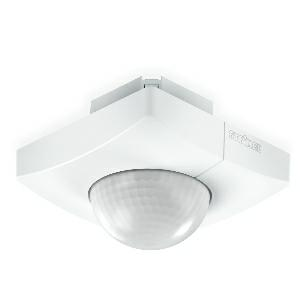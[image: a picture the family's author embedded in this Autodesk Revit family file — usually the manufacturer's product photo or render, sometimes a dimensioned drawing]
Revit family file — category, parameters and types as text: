
# Revit family: is_3360_057244
name_source: partatom
category: Elektroinstallationen
revit_build: Autodesk Revit 2016 (Build: 20190508_0715(x64)
units: mm (PartAtom-declared; Revit-internal decimal feet)

## family parameters
Basisbauteil = Fläche
Beim Laden mit Abzugskörper schneiden = Nein
Bemaßung runder Anschluss = Durchmesser verwenden
Beschriftungsausrichtung beibehalten = Nein
Gemeinsam genutzt = Nein
Raumberechnungspunkt = Nein
Teiletyp = Normal

## types (1)
- IS 3360
    Apparent Load = 0 VA
    Beschreibung = Type: Motion detectors; Dimensions (L x W x H): 78 x 94 x 94 mm; Mains power supply: 12 – 22,5 V / 50 – 60 Hz; Sensor Technology: passive infrared; Application, place: Indoors; Application, room: production facilities, recreation room, changing room, function room / ancillary room, sports hall, reception / lobby, stairwell, WC / washroom, multi-storey / underground car park, warehouse, Indoors; Installation site: ceiling; Installation: Concealed wiring; Switching zones: 448 switching zones; Electronic scalability: No; Mechanical scalability: No; Mounting height: 2,5 – 4,00 m; Optimum mounting height: 2,8 m; Detection angle: 360 °; Angle of aperture: 45 °; Sneak-by guard: Yes; Capability of masking out individual segments: Yes; Reach, radial: Ø 8 m (50 m²); Reach, tangential: Ø 40 m (1257 m²); Reach, presence: Ø 3 m (7 m²); Twilight setting TEACH: Yes; Twilight setting: 2 – 1000 lx; Switching output 1, floating: No; Control output, Dali: Addressable/slave; Basic light level function: No; With bus coupling: Yes; Settings via: Bus; With remote control: No; Interconnection: Yes; IP-rating: IP20; Material: Plastic; Ambient temperature: -20 – 50 °C; Colour: white; Colour, RAL: 9003; Manufacturer's Warranty: 5 years; Version: DALI-2 IPD - concealed, sq.; PU1, EAN: 4007841057244
    Height = 0 mm  [stored 0 ft]
    Hersteller = Steinel
    Length = 78 mm  [stored 0.255906 ft]
    Maximum range = 20.158 m
    ModVariant = Nein
    Modell = 057244
    Mounting Place = Ceiling
    Mounting Type = Recessed
    Number of Poles = 1
    OnlyDefault = Ja
    Power Factor = 1
    Product Name = IS 3360
    Product group = Presence detector
    ProductGroupID = 4
    Protection Class = Protection class
    Protection Degree = IP 20
    RlxData = <blob elided: 158649 chars, md5=93a487e7>
    Sensor characteristics = Circular 300°-360°
    Sensor type = Passive (infrared)
    SensorDataFile = <blob elided: 6785 chars, md5=23016e95>
    Type of entry = Presence, Motion
    Typenbild = produkt1_057244.jpg
    Typenkommentare = Product without accessories
    URL = http://relux.com
    VarID = ---
    Voltage = 0 V
    Vorgabe-Ansicht = 1800 mm
    Weight = 0.00 kg
    Width = 94 mm  [stored 0.308399 ft]

note: [stored X ft] marks values corroborated as IEEE doubles in the binary element streams (Revit-internal decimal feet)

## geometry (parser evidence)
native form markers: Blend x4, Sweep x16
no freeform markers — native parametric forms only
